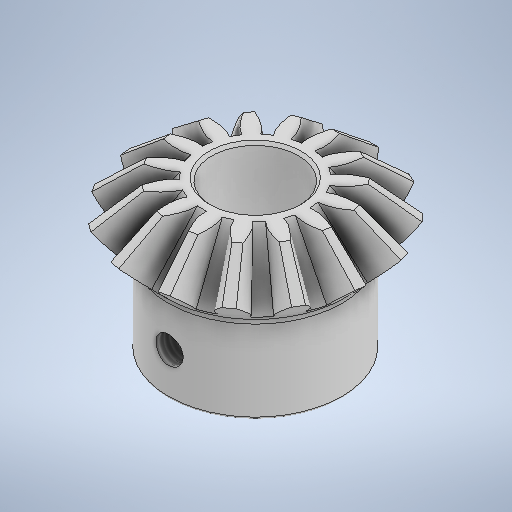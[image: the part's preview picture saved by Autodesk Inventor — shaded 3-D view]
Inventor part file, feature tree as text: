
AUTODESK INVENTOR PART (.ipt)
format: ipt  version: 2025.1 (Build 291241000, 241)  size: 791,040 bytes
history: native  units: in
note: dims shown in document units (in); Inventor stores cm internally (conversion verified against a paired STEP export)
features: plane x1, hole x1, sketch x1
ambient origin geometry x8: Origin, YZ Plane, XZ Plane, XY Plane, X Axis, Y Axis, Z Axis, Center Point
bodies: Solid1 (feature_tree)
feature tree (3):
  plane  "Work Plane1"
  hole  "Hole1"  [1 undecoded]
  sketch  "Sketch1"  dims[d0=0.156in d1=0.38in d2=0.375in d3=0.25in d4=0.5635in d5=0.411in d6=0.8108in]
note: 1 required parameter value undecoded (feature->parameter linkage not recoverable at this tier; creation-order binding heuristic only, values carry confidence <= 0.55)
